# Revit family: Building-Materials_Glass-Glazing_Vitro-Architectural-Glass_SOLARBAN-72
name_source: partatom
category: Curtain Panels
units: mm (PartAtom-declared; Revit-internal decimal feet)

## family parameters
Always vertical = Yes
Classification Number = 23.25.20.14.11.11.17
Cut with Voids When Loaded = No
Shared = No

## types (2) — shared parameters
1st Lite Thickness = 0' - 0 1/4"
2nd Lite Thickness = 0' - 0 1/4"
Airspace Thickness = 0' - 0 1/2"
Analytic Construction = Low-E double glazing (1/4 in + 1/4 in)
Assembly Code = B2020220
Define Thermal Properties by = Schematic Type
Description = Solarban® 72 glass provides high visible light transmittance (VLT), exceptional clarity and superior solar control performance. The exceptionally clear aesthetic makes it the ideal choice for both interior and exterior applications, such as vision and spandrel glass.
Finish = Glass
Heat Transfer Coefficient (U) = 0.29 BTU/(h·ft²·°F)
Keynote = 08900
Manufacturer = Vitro Architectural Glass
Product Guid = b0a5e737-cc59-4a7b-9f32-c2b4f36f3ffc
Product Page URL = https://www.vitroglazings.com
Product data url = https://www.bimobject.com
Reflectance (Visible Exterior) = 13
Reflectance (Visible Interior) = 14
Shadow Coefficient = 0.32
Solar Heat Gain Coefficient = 0.28
Thermal Resistance (R) = 8.3333 (h·ft²·°F)/BTU
Total Thickness = 0' - 1"
U-Value Air (Summer Day) = 0.26 BTU/(h·ft²·°F)
U-Value Air (Winter Night) = 0.28 BTU/(h·ft²·°F)
U-Value Argon (Summer Day) = 0.21 BTU/(h·ft²·°F)
U-Value Argon (Winter Night) = 0.24 BTU/(h·ft²·°F)
URL = https://www.vitroglazings.com

## per-type parameters (varying)
| type | Exterior Glass Material | Glass Code | ISO Damage Weighted Transmittance | Interior Glass Material | Light to Solar Gain | Solar Light Transmittance | UV Light Transmittance | Visual Light Transmittance |
| Solarban 72 (2) Starphire + Starphire | Vitro Architectural-Glass - Solarban 72 (2) Starphire | 2 | 0.471 | Vitro Architectural-Glass - Starphire | 2.43 | 0.26 | 0.9 | 0.68 |
| Solarban 72 (2) Acuity + Acuity | Vitro Architectural-Glass - Solarban 72 (2) Acuity | 3 | 0.462 | Vitro Architectural-Glass - Acuity | 2.39 | 0.25 | 0.8 | 0.67 |

note: column(s) folded — value = type name in every type: Model

## geometry (parser evidence)
native form markers: Sweep x1
no freeform markers — native parametric forms only
